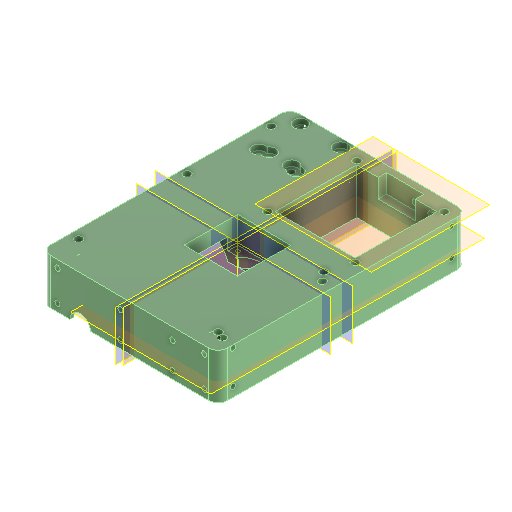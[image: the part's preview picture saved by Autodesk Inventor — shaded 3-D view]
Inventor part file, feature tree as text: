
AUTODESK INVENTOR PART (.ipt)
format: ipt  version: 2024.1 (Build 281209000, 209)  size: 596,480 bytes
history: native  units: mm
features: plane x7, other x4, sketch x3
ambient origin geometry x8: Origin, YZ Plane, XZ Plane, XY Plane, X Axis, Y Axis, Z Axis, Center Point
bodies: Volumenkörper1 (feature_tree)
feature tree (14):
  other  "60_Planktoscope_Base_half_wormdrive_1.ipt"
  other  "Volumenkörper1::60_Planktoscope_Base_half_wormdrive_1.ipt"
  other  "Bezeichnung1"
  sketch  "Skizze1"  dims[d0=10.0mm]
  sketch  "Skizze2"
  sketch  "Skizze17"
  plane  "Arbeitsebene1"
  plane  "Arbeitsebene2"
  plane  "Arbeitsebene3"
  plane  "Arbeitsebene4"
  plane  "Arbeitsebene5"
  plane  "Arbeitsebene6"
  plane  "Arbeitsebene7"
  other  "Arbeitsachse1"
